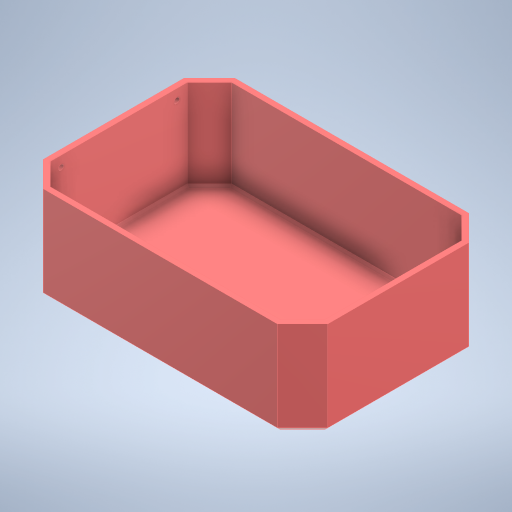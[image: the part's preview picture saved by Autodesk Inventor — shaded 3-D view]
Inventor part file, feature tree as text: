
AUTODESK INVENTOR PART (.ipt)
format: ipt  version: 2024 (Build 280153000, 153)  size: 296,448 bytes
history: native  units: in
note: dims shown in document units (in); Inventor stores cm internally (conversion verified against a paired STEP export)
features: sketch x4, extrude x3, plane x1, chamfer x1, delete_face x1, thicken_offset x1, projected_geometry x1
ambient origin geometry x8: Origin, YZ Plane, XZ Plane, XY Plane, X Axis, Y Axis, Z Axis, Center Point
bodies: Body1 (feature_tree)
feature tree (12):
  plane  "Work Plane1"
  extrude  "Extrusion3"  Depth=26.9in
  chamfer  "Chamfer1"  Distance=9.0in
  delete_face  "Delete Face3"
  thicken_offset  "Thicken3"
  sketch  "Sketch8"  dims[d20=18.1in]
  extrude  "Extrusion6"  Depth=0.5in
  extrude  "Extrusion7"  Depth=0.5in
  sketch  "Sketch7"  dims[d3=8.5in d19=26.9in]
  projected_geometry  "Projected Loop3"
  sketch  "Sketch12"  dims[d21=135.0deg d22=9.0in d23=0.0in]
  sketch  "Sketch13"  dims[d24=0.5in d25=0.125in d26=45.0deg d27=0.5in d40=1.0in d41=1.0in d42=1.0in d43=1.0in d44=0.5in d45=0.5in d46=1.0in d47=0.0in d48=1.0in d49=0.5in d50=1.0in d51=0.0in]
